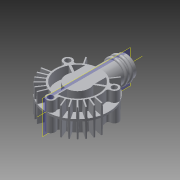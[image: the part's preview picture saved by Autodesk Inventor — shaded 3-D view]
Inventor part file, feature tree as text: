
AUTODESK INVENTOR PART (.ipt)
format: ipt  version: 2018 (Build 220112000, 112)  size: 2,390,016 bytes
history: native  units: in
note: dims shown in document units (in); Inventor stores cm internally (conversion verified against a paired STEP export)
features: sketch x24, extrude x21, pattern_circular x9, plane x4, draft x4, mirror x3, fillet x2, hole x2, revolve x2, other x1, thread x1
ambient origin geometry x8: Origin, YZ Plane, XZ Plane, XY Plane, X Axis, Y Axis, Z Axis, Center Point
bodies: Solid1 (feature_tree)
feature tree (73):
  extrude  "Extrusion1"  Depth=0.05in TaperAngle=0.0deg
  extrude  "Extrusion2"  Depth=1.08in
  extrude  "Extrusion3"  Depth=0.5in
  pattern_circular  "Circular Pattern1"  Count=3 Angle=360.0deg
  plane  "Work Plane2"
  extrude  "Extrusion17"  Depth=0.25in TaperAngle=0.0deg
  extrude  "Extrusion20"  Depth=0.25in
  draft  "FaceDraft5"
  draft  "FaceDraft6"
  fillet  "Fillet6"  Radius=0.125in
  pattern_circular  "Circular Pattern7"  Count=3 Angle=360.0deg
  extrude  "Extrusion21"  Depth=0.25in TaperAngle=360.0deg
  pattern_circular  "Circular Pattern8"  [2 undecoded]
  extrude  "Extrusion22"  Depth=0.25in
  draft  "FaceDraft7"
  draft  "FaceDraft8"
  fillet  "Fillet7"  Radius=0.125in
  pattern_circular  "Circular Pattern9"  [2 undecoded]
  extrude  "Extrusion23"  Depth=0.25in
  pattern_circular  "Circular Pattern10"  [2 undecoded]
  hole  "Hole1"  [1 undecoded]
  pattern_circular  "Circular Pattern11"  [2 undecoded]
  extrude  "Extrusion24"  Depth=0.25in
  plane  "Work Plane5"
  extrude  "Extrusion25"  Depth=0.25in TaperAngle=0.0deg
  hole  "Hole2"  [1 undecoded]
  other  "Work Axis1"
  revolve  "Revolution2"  [1 undecoded]
  pattern_circular  "Circular Pattern2"  [2 undecoded]
  extrude  "Extrusion5"  Depth=0.25in TaperAngle=360.0deg
  extrude  "Extrusion6"  Depth=0.25in
  mirror  "Mirror1"
  mirror  "Mirror2"
  extrude  "Extrusion7"  Depth=0.25in
  extrude  "Extrusion8"  Depth=0.25in TaperAngle=0.0deg
  extrude  "Extrusion9"  Depth=0.25in TaperAngle=360.0deg
  pattern_circular  "Circular Pattern3"  [2 undecoded]
  mirror  "Mirror3"
  extrude  "Extrusion10"  Depth=0.25in
  pattern_circular  "Circular Pattern4"  [2 undecoded]
  extrude  "Extrusion11"  Depth=0.25in
  plane  "Work Plane1"
  extrude  "Extrusion12"  Depth=0.25in TaperAngle=360.0deg
  extrude  "Extrusion13"  Depth=0.25in TaperAngle=0.0deg
  revolve  "Revolution1"  Angle=360.0deg
  extrude  "Extrusion14"  Depth=0.25in
  extrude  "Extrusion16"  Depth=0.25in TaperAngle=360.0deg
  thread  "Thread1"  [1 undecoded]
  sketch  "Sketch1"  dims[d0=1.5in d1=0.05in d2=0.0in]
  sketch  "Sketch2"  dims[d3=1.0in d4=1.08in]
  sketch  "Sketch3"  dims[d5=0.5625in d6=0.5in]
  sketch  "Sketch5"  dims[d7=0.25in d8=0.0in]
  sketch  "Sketch6"  dims[d9=0.05in]
  sketch  "Sketch7"  dims[d10=0.25in d11=0.0in d12=1.1811in d13=360.0deg]
  sketch  "Sketch8"  dims[d20=11.0236in d21=360.0deg d23=0.25in d24=0.0in]
  sketch  "Sketch9"  dims[d25=0.25in d26=0.0in d27=0.5in d28=0.125in d29=0.0in]
  sketch  "Sketch10"  dims[d30=1.0in]
  sketch  "Sketch11"  dims[d31=0.25in d32=0.0in]
  sketch  "Sketch12"  dims[d35=0.25in]
  sketch  "Sketch13"  dims[d36=0.2in]
  sketch  "Sketch14"  dims[d37=0.25in d38=0.0in d39=1.1811in d40=360.0deg]
  sketch  "Sketch15"  dims[d42=0.25in d43=0.0in d44=1.1811in d45=360.0deg]
  sketch  "Sketch17"  dims[d47=0.25in d48=0.0in]
  sketch  "Sketch18"  dims[d49=0.5in]
  sketch  "Sketch20"  dims[d50=0.0625in d51=0.625in d52=0.0in d53=0.0in]
  sketch  "Sketch21"  dims[d54=0.25in d55=0.0in]
  sketch  "Sketch22"  dims[d57=0.1in]
  sketch  "Sketch23"  dims[d58=0.1in]
  sketch  "Sketch24"  dims[d59=0.05in]
  plane  "Work Plane4"
  sketch  "Sketch26"  dims[d60=0.25in]
  sketch  "Sketch27"  dims[d61=0.5in]
  sketch  "Sketch28"  dims[d62=90.0deg d63=0.75in d64=0.0in d67=0.2in d68=0.125in d69=0.0in d70=1.0in d71=0.0in d72=0.25in d76=0.375in d77=0.0in d106=22.5deg d107=0.025in d108=0.025in d109=0.25in d110=0.0in d111=0.0137in d112=0.0137in d113=0.01in d114=12.5984in d115=360.0deg d117=0.1in d118=0.1in d119=0.25in d120=0.0in d121=1.1811in d122=360.0deg d124=0.25in d125=0.0in d126=0.0103in d127=0.0103in d128=0.01in d129=12.5984in d130=360.0deg d132=0.25in d133=0.0in d134=1.1811in d135=360.0deg d137=1.0in d138=1.0in d139=0.129in d140=0.75in d141=0.219in d142=0.112in d143=0.5635in d144=1.0in d145=0.8108in d146=1.1811in d147=360.0deg d149=0.125in d150=0.0in d152=-0.625in d153=0.5in d154=0.5625in d155=0.0in d156=0.313in d157=0.236in d158=0.0246in d159=0.329in d160=0.219in d161=0.112in d162=0.5635in d163=0.25in d164=0.8108in d165=0.125in d166=0.25in d167=90.0deg]
note: 18 required parameter values undecoded (feature->parameter linkage not recoverable at this tier; creation-order binding heuristic only, values carry confidence <= 0.55)